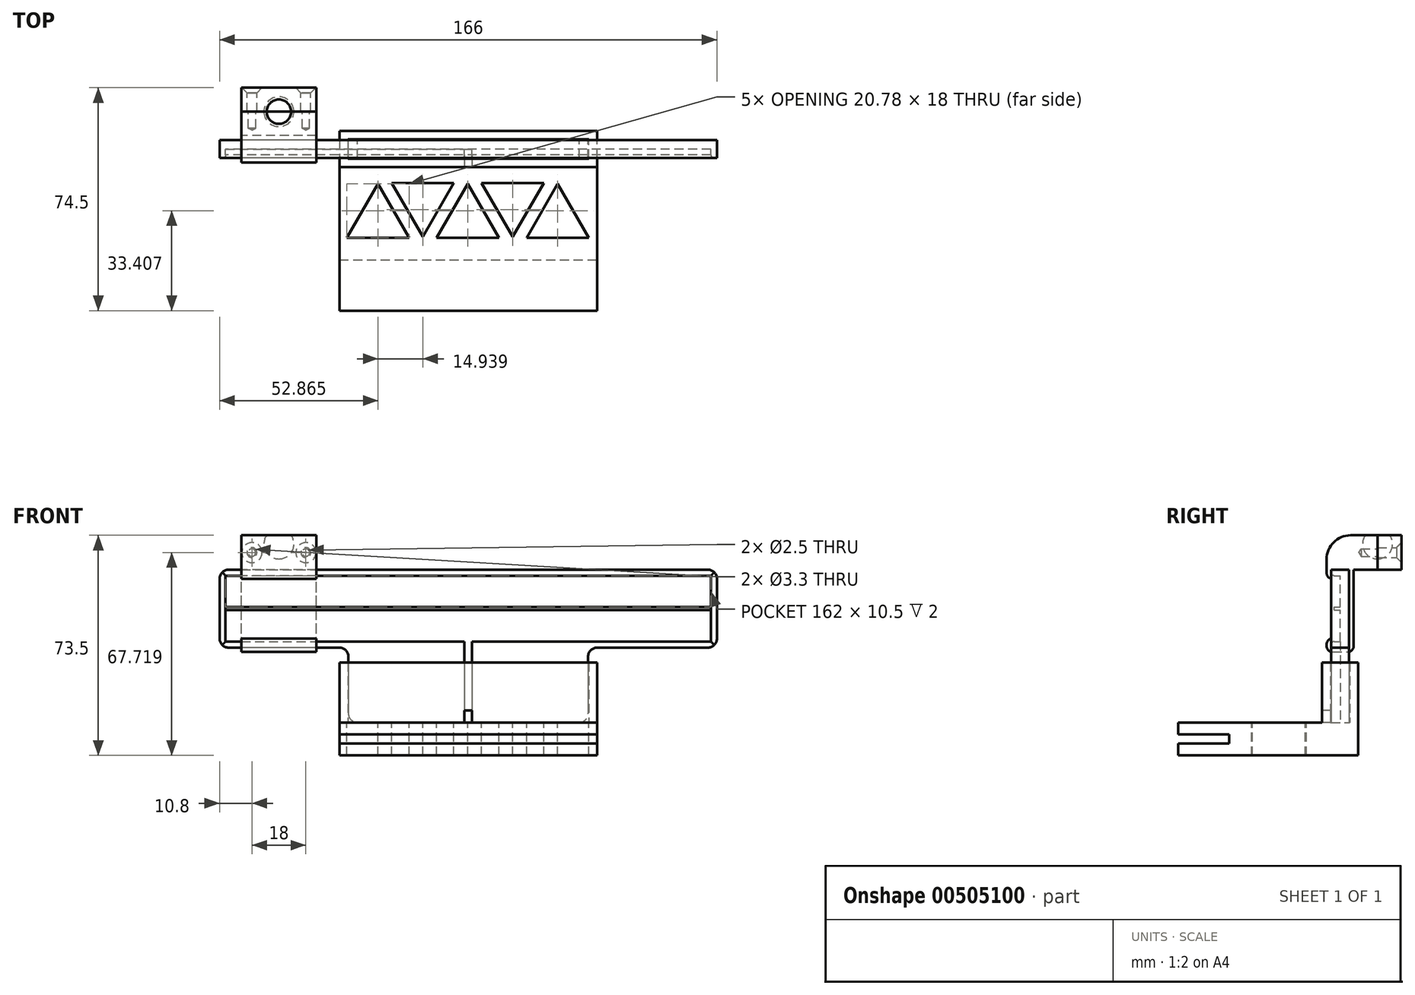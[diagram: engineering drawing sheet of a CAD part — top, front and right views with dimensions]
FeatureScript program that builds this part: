
annotation { "Feature Type Name" : "Feature", "Feature Type Description" : "" }
export const myFeature = defineFeature(function(context is Context, id is Id, definition is map)
    precondition{}
    {
        {
            var Q0;
            Q0=qCreatedBy(makeId("Front.planeOp"),FACE);
            var sketch = newSketch(context, id + "F0", { "sketchPlane" : qUnion([Q0])});
            skLineSegment(sketch, "E0.bottom", {"start": v(83, -13) * mm, "end": v(-83, -13) * mm});
            skLineSegment(sketch, "E0.top", {"start": v(83, 13) * mm, "end": v(-83, 13) * mm});
            skLineSegment(sketch, "E0.left", {"start": v(83, -13) * mm, "end": v(83, 13) * mm});
            skLineSegment(sketch, "E0.right", {"start": v(-83, -13) * mm, "end": v(-83, 13) * mm});
            skPoint(sketch, "E0.middle", {"position": v(0, 0) * mm});
            skLineSegment(sketch, "E1.bottom", {"start": v(-40, -13) * mm, "end": v(40, -13) * mm});
            skLineSegment(sketch, "E1.top", {"start": v(-40, -38) * mm, "end": v(40, -38) * mm});
            skLineSegment(sketch, "E1.left", {"start": v(-40, -13) * mm, "end": v(-40, -38) * mm});
            skLineSegment(sketch, "E1.right", {"start": v(40, -13) * mm, "end": v(40, -38) * mm});
            skSolve(sketch);
        }
        {
            var Q0;
            Q0 = qSketchRegion(id + "F0", true);
            extrude(context, id + "F1", {"entities" : qUnion([Q0]), "depth" : 3 * mm});
        }
        {
            var Q0;
            Q0=makeQuery(id+"F1.opExtrude","CAP_FACE",FACE,{"disambiguationData":[OSD([sQuery(id+"F0.wireOp",EDGE,"E0.bottom"),sQuery(id+"F0.wireOp",EDGE,"E0.top"),sQuery(id+"F0.wireOp",EDGE,"E0.left"),sQuery(id+"F0.wireOp",EDGE,"E0.right"),sQuery(id+"F0.wireOp",EDGE,"ytznH25m-S5ns-YEqi-e5KJ-ufFRk47Cag2v.top"),sQuery(id+"F0.wireOp",EDGE,"ytznH25m-S5ns-YEqi-e5KJ-ufFRk47Cag2v.left"),sQuery(id+"F0.wireOp",EDGE,"ytznH25m-S5ns-YEqi-e5KJ-ufFRk47Cag2v.right"),sQuery(id+"F0.wireOp",EDGE,"df92ae9d-98ef-4524-ba73-5d8abbe1a62c0.MirrorCS"),sQuery(id+"F0.wireOp",EDGE,"cedffd24-c050-4cca-8132-216843a770b10.MirrorCS"),sQuery(id+"F0.wireOp",EDGE,"234c480e-fd0d-4cc7-8f42-385ae9078e1c0.MirrorCS")])],"isStart":false});
            var sketch = newSketch(context, id + "F2", { "sketchPlane" : qUnion([Q0])});
            skLineSegment(sketch, "E2.0", {"start": v(83, 13) * mm, "end": v(-83, 13) * mm});
            skLineSegment(sketch, "E3.0", {"start": v(-83, -13) * mm, "end": v(-83, 13) * mm});
            skLineSegment(sketch, "E4.0", {"start": v(-40, -13) * mm, "end": v(-83, -13) * mm});
            skLineSegment(sketch, "E5.0", {"start": v(83, -13) * mm, "end": v(40, -13) * mm});
            skLineSegment(sketch, "E6.0", {"start": v(83, -13) * mm, "end": v(83, 13) * mm});
            skLineSegment(sketch, "E7.0", {"start": v(40, -13) * mm, "end": v(40, -38) * mm});
            skLineSegment(sketch, "E8.0", {"start": v(-40, -13) * mm, "end": v(-40, -38) * mm});
            skLineSegment(sketch, "E9.0", {"start": v(-40, -11) * mm, "end": v(-81, -11) * mm});
            skLineSegment(sketch, "E9.1", {"start": v(81, -11) * mm, "end": v(40, -11) * mm});
            skLineSegment(sketch, "E9.2", {"start": v(81, -11) * mm, "end": v(81, 11) * mm});
            skLineSegment(sketch, "E9.3", {"start": v(81, 11) * mm, "end": v(-81, 11) * mm});
            skLineSegment(sketch, "E9.4", {"start": v(-81, -11) * mm, "end": v(-81, 11) * mm});
            skLineSegment(sketch, "E10", {"start": v(-40, -11) * mm, "end": v(-1.25, -11) * mm});
            skLineSegment(sketch, "E11", {"start": v(-1.25, -11) * mm, "end": v(-1.25, -38) * mm});
            skLineSegment(sketch, "E12", {"start": v(-1.25, -38) * mm, "end": v(-40, -38) * mm});
            skLineSegment(sketch, "E13", {"start": v(40, -11) * mm, "end": v(1.25, -11) * mm});
            skLineSegment(sketch, "E14", {"start": v(1.25, -11) * mm, "end": v(1.25, -38) * mm});
            skLineSegment(sketch, "E15", {"start": v(1.25, -38) * mm, "end": v(40, -38) * mm});
            skSolve(sketch);
        }
        {
            var Q0;
            Q0 = qSketchRegion(id + "F2", true);
            extrude(context, id + "F3", {"entities" : qUnion([Q0]), "operationType" : NewBodyOperationType.ADD, "depth" : 3 * mm});
        }
        {
            var Q0;
            Q0=makeQuery(id+"F1.opExtrude","CAP_FACE",FACE,{"disambiguationData":[OSD([sQuery(id+"F0.wireOp",EDGE,"E0.bottom"),sQuery(id+"F0.wireOp",EDGE,"E0.top"),sQuery(id+"F0.wireOp",EDGE,"E0.left"),sQuery(id+"F0.wireOp",EDGE,"E0.right"),sQuery(id+"F0.wireOp",EDGE,"E1.top"),sQuery(id+"F0.wireOp",EDGE,"E1.left"),sQuery(id+"F0.wireOp",EDGE,"E1.right")])],"isStart":false});
            var sketch = newSketch(context, id + "F4", { "sketchPlane" : qUnion([Q0])});
            skLineSegment(sketch, "E16.bottom", {"start": v(81, -0.5) * mm, "end": v(-81, -0.5) * mm});
            skLineSegment(sketch, "E16.top", {"start": v(81, 0.5) * mm, "end": v(-81, 0.5) * mm});
            skLineSegment(sketch, "E16.left", {"start": v(81, -0.5) * mm, "end": v(81, 0.5) * mm});
            skLineSegment(sketch, "E16.right", {"start": v(-81, -0.5) * mm, "end": v(-81, 0.5) * mm});
            skPoint(sketch, "E16.middle", {"position": v(0, 0) * mm});
            skSolve(sketch);
        }
        {
            var Q0;
            Q0 = qSketchRegion(id + "F4", true);
            extrude(context, id + "F5", {"entities" : qUnion([Q0]), "operationType" : NewBodyOperationType.ADD, "depth" : 2 * mm});
        }
        {
            var Q0;
            Q0=makeQuery(id+"F3.boolean.opBoolean","MERGE",EDGE,{"derivedFrom":[makeQuery(id+"F1.opExtrude","SWEPT_EDGE",EDGE,{"disambiguationData":[OSD([sQuery(id+"F0.wireOp",EDGE,"E0.top"),sQuery(id+"F0.wireOp",EDGE,"E0.left")])]}),makeQuery(id+"F3.opExtrude","SWEPT_EDGE",EDGE,{"disambiguationData":[OSD([sQuery(id+"F2.wireOp",EDGE,"E2.0"),sQuery(id+"F2.wireOp",EDGE,"E6.0")])]})]});
            var Q1;
            Q1=makeQuery(id+"F3.boolean.opBoolean","MERGE",EDGE,{"derivedFrom":[makeQuery(id+"F1.opExtrude","SWEPT_EDGE",EDGE,{"disambiguationData":[OSD([sQuery(id+"F0.wireOp",EDGE,"E0.bottom"),sQuery(id+"F0.wireOp",EDGE,"E0.left")])]}),makeQuery(id+"F3.opExtrude","SWEPT_EDGE",EDGE,{"disambiguationData":[OSD([sQuery(id+"F2.wireOp",EDGE,"E5.0"),sQuery(id+"F2.wireOp",EDGE,"E6.0")])]})]});
            var Q2;
            Q2=makeQuery(id+"F3.boolean.opBoolean","MERGE",EDGE,{"derivedFrom":[makeQuery(id+"F1.opExtrude","SWEPT_EDGE",EDGE,{"disambiguationData":[OSD([sQuery(id+"F0.wireOp",EDGE,"E0.bottom"),sQuery(id+"F0.wireOp",EDGE,"E1.bottom"),sQuery(id+"F0.wireOp",EDGE,"E1.right")])]}),makeQuery(id+"F3.opExtrude","SWEPT_EDGE",EDGE,{"disambiguationData":[OSD([sQuery(id+"F2.wireOp",EDGE,"E5.0"),sQuery(id+"F2.wireOp",EDGE,"E7.0")])]})]});
            var Q3;
            Q3=makeQuery(id+"F3.boolean.opBoolean","MERGE",EDGE,{"derivedFrom":[makeQuery(id+"F1.opExtrude","SWEPT_EDGE",EDGE,{"disambiguationData":[OSD([sQuery(id+"F0.wireOp",EDGE,"E0.bottom"),sQuery(id+"F0.wireOp",EDGE,"E1.bottom"),sQuery(id+"F0.wireOp",EDGE,"E1.left")])]}),makeQuery(id+"F3.opExtrude","SWEPT_EDGE",EDGE,{"disambiguationData":[OSD([sQuery(id+"F2.wireOp",EDGE,"E4.0"),sQuery(id+"F2.wireOp",EDGE,"E8.0")])]})]});
            var Q4;
            Q4=makeQuery(id+"F3.boolean.opBoolean","MERGE",EDGE,{"derivedFrom":[makeQuery(id+"F1.opExtrude","SWEPT_EDGE",EDGE,{"disambiguationData":[OSD([sQuery(id+"F0.wireOp",EDGE,"E0.bottom"),sQuery(id+"F0.wireOp",EDGE,"E0.right")])]}),makeQuery(id+"F3.opExtrude","SWEPT_EDGE",EDGE,{"disambiguationData":[OSD([sQuery(id+"F2.wireOp",EDGE,"E3.0"),sQuery(id+"F2.wireOp",EDGE,"E4.0")])]})]});
            var Q5;
            Q5=makeQuery(id+"F3.boolean.opBoolean","MERGE",EDGE,{"derivedFrom":[makeQuery(id+"F1.opExtrude","SWEPT_EDGE",EDGE,{"disambiguationData":[OSD([sQuery(id+"F0.wireOp",EDGE,"E0.top"),sQuery(id+"F0.wireOp",EDGE,"E0.right")])]}),makeQuery(id+"F3.opExtrude","SWEPT_EDGE",EDGE,{"disambiguationData":[OSD([sQuery(id+"F2.wireOp",EDGE,"E2.0"),sQuery(id+"F2.wireOp",EDGE,"E3.0")])]})]});
            var Q6;
            Q6=makeQuery(id+"F3.boolean.opBoolean","MERGE",EDGE,{"derivedFrom":[makeQuery(id+"F1.opExtrude","SWEPT_EDGE",EDGE,{"disambiguationData":[OSD([sQuery(id+"F0.wireOp",EDGE,"E1.top"),sQuery(id+"F0.wireOp",EDGE,"E1.right")])]}),makeQuery(id+"F3.opExtrude","SWEPT_EDGE",EDGE,{"disambiguationData":[OSD([sQuery(id+"F2.wireOp",EDGE,"E7.0"),sQuery(id+"F2.wireOp",EDGE,"E15")])]})]});
            var Q7;
            Q7=makeQuery(id+"F3.boolean.opBoolean","MERGE",EDGE,{"derivedFrom":[makeQuery(id+"F1.opExtrude","SWEPT_EDGE",EDGE,{"disambiguationData":[OSD([sQuery(id+"F0.wireOp",EDGE,"E1.top"),sQuery(id+"F0.wireOp",EDGE,"E1.left")])]}),makeQuery(id+"F3.opExtrude","SWEPT_EDGE",EDGE,{"disambiguationData":[OSD([sQuery(id+"F2.wireOp",EDGE,"E8.0"),sQuery(id+"F2.wireOp",EDGE,"E12")])]})]});
            fillet(context, id + "F6", {"entities" : qUnion([Q0, Q1, Q2, Q3, Q4, Q5, Q6, Q7]), "radius" : 3 * mm, "tangentPropagation" : true, "allowEdgeOverflow" : false});
        }
        {
            var Q0;
            Q0=makeQuery(id+"F3.opExtrude","CAP_EDGE",EDGE,{"disambiguationData":[OSD([sQuery(id+"F2.wireOp",EDGE,"E9.3")])],"isStart":false});
            var Q1;
            Q1=makeQuery(id+"F3.opExtrude","CAP_EDGE",EDGE,{"disambiguationData":[OSD([sQuery(id+"F2.wireOp",EDGE,"E9.4")])],"isStart":false});
            var Q2;
            Q2=makeQuery(id+"F3.opExtrude","CAP_EDGE",EDGE,{"disambiguationData":[OSD([sQuery(id+"F2.wireOp",EDGE,"E9.0"),sQuery(id+"F2.wireOp",EDGE,"E10")])],"isStart":false});
            var Q3;
            Q3=makeQuery(id+"F3.opExtrude","CAP_EDGE",EDGE,{"disambiguationData":[OSD([sQuery(id+"F2.wireOp",EDGE,"E9.1"),sQuery(id+"F2.wireOp",EDGE,"E13")])],"isStart":false});
            var Q4;
            Q4=makeQuery(id+"F3.opExtrude","CAP_EDGE",EDGE,{"disambiguationData":[OSD([sQuery(id+"F2.wireOp",EDGE,"E9.2")])],"isStart":false});
            fillet(context, id + "F7", {"entities" : qUnion([Q0, Q1, Q2, Q3, Q4]), "radius" : 1 * mm, "tangentPropagation" : true, "allowEdgeOverflow" : false});
        }
        {
            var Q0;
            Q0=makeQuery(id+"F3.boolean.opBoolean","MERGE",FACE,{"derivedFrom":[makeQuery(id+"F1.opExtrude","SWEPT_FACE",FACE,{"disambiguationData":[OSD([sQuery(id+"F0.wireOp",EDGE,"E1.top")])]}),makeQuery(id+"F3.opExtrude","SWEPT_FACE",FACE,{"disambiguationData":[OSD([sQuery(id+"F2.wireOp",EDGE,"E12")])]}),makeQuery(id+"F3.opExtrude","SWEPT_FACE",FACE,{"disambiguationData":[OSD([sQuery(id+"F2.wireOp",EDGE,"E15")])]})]});
            var sketch = newSketch(context, id + "F8", { "sketchPlane" : qUnion([Q0])});
            skLineSegment(sketch, "E17.0", {"start": v(1.25, 9) * mm, "end": v(37, 9) * mm});
            skLineSegment(sketch, "E17.1", {"start": v(1.25, 9) * mm, "end": v(-1.25, 9) * mm});
            skLineSegment(sketch, "E17.2", {"start": v(37, 9) * mm, "end": v(43, 9) * mm});
            skLineSegment(sketch, "E17.3", {"start": v(-37, 9) * mm, "end": v(-1.25, 9) * mm});
            skLineSegment(sketch, "E17.4", {"start": v(-43, 9) * mm, "end": v(-37, 9) * mm});
            skLineSegment(sketch, "E17.5", {"start": v(-43, -3) * mm, "end": v(-43, 9) * mm});
            skLineSegment(sketch, "E17.6", {"start": v(43, 9) * mm, "end": v(43, -3) * mm});
            skLineSegment(sketch, "E17.7", {"start": v(43, -3) * mm, "end": v(37, -3) * mm});
            skLineSegment(sketch, "E17.8", {"start": v(-37, -3) * mm, "end": v(37, -3) * mm});
            skLineSegment(sketch, "E17.9", {"start": v(-37, -3) * mm, "end": v(-43, -3) * mm});
            skLineSegment(sketch, "E18.0", {"start": v(-37, 6.2) * mm, "end": v(-1.25, 6.2) * mm});
            skLineSegment(sketch, "E18.1", {"start": v(-40.2, 6.2) * mm, "end": v(-37, 6.2) * mm});
            skLineSegment(sketch, "E18.2", {"start": v(-40.2, -0.2) * mm, "end": v(-40.2, 6.2) * mm});
            skLineSegment(sketch, "E18.3", {"start": v(-37, -0.2) * mm, "end": v(-40.2, -0.2) * mm});
            skLineSegment(sketch, "E18.4", {"start": v(-37, -0.2) * mm, "end": v(37, -0.2) * mm});
            skLineSegment(sketch, "E18.5", {"start": v(1.25, 6.2) * mm, "end": v(37, 6.2) * mm});
            skLineSegment(sketch, "E18.6", {"start": v(37, 6.2) * mm, "end": v(40.2, 6.2) * mm});
            skLineSegment(sketch, "E18.7", {"start": v(40.2, 6.2) * mm, "end": v(40.2, -0.2) * mm});
            skLineSegment(sketch, "E18.8", {"start": v(40.2, -0.2) * mm, "end": v(37, -0.2) * mm});
            skLineSegment(sketch, "E19", {"start": v(1.25, 6.2) * mm, "end": v(-1.25, 6.2) * mm});
            skSolve(sketch);
        }
        {
            var Q0;
            Q0 = qSketchRegion(id + "F8", true);
            extrude(context, id + "F9", {"entities" : qUnion([Q0]), "oppositeDirection" : true, "depth" : 20 * mm});
        }
        {
            var Q0;
            Q0=makeQuery(id+"F9.opExtrude","CAP_FACE",FACE,{"disambiguationData":[OSD([sQuery(id+"F8.wireOp",EDGE,"8f80f519-4c1a-4023-b6a8-295c1c52ba16.0"),sQuery(id+"F8.wireOp",EDGE,"08e55738-1a8b-462c-8b5f-6e2352a6861a.0"),sQuery(id+"F8.wireOp",EDGE,"df1ae1b3-9407-48c6-8a92-31e4def18985.0"),sQuery(id+"F8.wireOp",EDGE,"7d09f095-180c-42f7-a629-e3ec4bffc7fb.0"),sQuery(id+"F8.wireOp",EDGE,"688b7f32-6940-423c-993a-f274958fdb2f.0"),sQuery(id+"F8.wireOp",EDGE,"d8653beb-2f90-41c1-82e6-8edcaac2620c.0"),sQuery(id+"F8.wireOp",EDGE,"a51acf63-bb40-4388-a766-018fd9339a70.0"),sQuery(id+"F8.wireOp",EDGE,"03a022a2-261d-486d-8482-124d5ba834bb.0"),sQuery(id+"F8.wireOp",EDGE,"Rfw31xpp-0EbB-aFLx-32cb-AFAiJERe9Qdi"),sQuery(id+"F8.wireOp",EDGE,"87e0dc2d-6d3b-407e-9d83-58cfb59100ee.0"),sQuery(id+"F8.wireOp",EDGE,"E17.0"),sQuery(id+"F8.wireOp",EDGE,"E17.1"),sQuery(id+"F8.wireOp",EDGE,"E17.2"),sQuery(id+"F8.wireOp",EDGE,"E17.3"),sQuery(id+"F8.wireOp",EDGE,"E17.4"),sQuery(id+"F8.wireOp",EDGE,"E17.5"),sQuery(id+"F8.wireOp",EDGE,"E17.6"),sQuery(id+"F8.wireOp",EDGE,"E17.7"),sQuery(id+"F8.wireOp",EDGE,"E17.8"),sQuery(id+"F8.wireOp",EDGE,"E17.9")])],"isStart":true});
            var sketch = newSketch(context, id + "F10", { "sketchPlane" : qUnion([Q0])});
            skLineSegment(sketch, "E20.0.0", {"start": v(-43, -3) * mm, "end": v(43, -3) * mm});
            skLineSegment(sketch, "E20.0.1", {"start": v(43, -3) * mm, "end": v(43, 9) * mm});
            skLineSegment(sketch, "E20.0.2", {"start": v(43, 9) * mm, "end": v(-43, 9) * mm});
            skLineSegment(sketch, "E20.0.3", {"start": v(-43, 9) * mm, "end": v(-43, -3) * mm});
            skSolve(sketch);
        }
        {
            var Q0;
            Q0 = qSketchRegion(id + "F10", true);
            extrude(context, id + "F11", {"entities" : qUnion([Q0]), "operationType" : NewBodyOperationType.ADD, "depth" : 2 * mm});
        }
        {
            var Q0;
            Q0=makeQuery(id+"F9.opExtrude","SWEPT_FACE",FACE,{"disambiguationData":[OSD([sQuery(id+"F8.wireOp",EDGE,"E17.0"),sQuery(id+"F8.wireOp",EDGE,"E17.1"),sQuery(id+"F8.wireOp",EDGE,"E17.2"),sQuery(id+"F8.wireOp",EDGE,"E17.3"),sQuery(id+"F8.wireOp",EDGE,"E17.4")])]});
            var sketch = newSketch(context, id + "F12", { "sketchPlane" : qUnion([Q0])});
            skPoint(sketch, "E21.0", {"position": v(1.25, -38) * mm});
            skPoint(sketch, "E22.0", {"position": v(-1.25, -38) * mm});
            skLineSegment(sketch, "E23.bottom", {"start": v(1.25, -38) * mm, "end": v(-1.25, -38) * mm});
            skLineSegment(sketch, "E23.top", {"start": v(1.25, -34) * mm, "end": v(-1.25, -34) * mm});
            skLineSegment(sketch, "E23.left", {"start": v(1.25, -38) * mm, "end": v(1.25, -34) * mm});
            skLineSegment(sketch, "E23.right", {"start": v(-1.25, -38) * mm, "end": v(-1.25, -34) * mm});
            skSolve(sketch);
        }
        {
            var Q0;
            Q0 = qSketchRegion(id + "F12", true);
            extrude(context, id + "F13", {"entities" : qUnion([Q0]), "operationType" : NewBodyOperationType.REMOVE, "oppositeDirection" : true, "depth" : 4 * mm});
        }
        {
            var Q0;
            Q0=makeQuery(id+"F11.opExtrude","CAP_FACE",FACE,{"disambiguationData":[OSD([sQuery(id+"F10.wireOp",EDGE,"E20.0.0"),sQuery(id+"F10.wireOp",EDGE,"E20.0.1"),sQuery(id+"F10.wireOp",EDGE,"E20.0.2"),sQuery(id+"F10.wireOp",EDGE,"E20.0.3")])],"isStart":false});
            var sketch = newSketch(context, id + "F14", { "sketchPlane" : qUnion([Q0])});
            skPoint(sketch, "E24.0", {"position": v(43, -3) * mm});
            skPoint(sketch, "E25.0", {"position": v(-43, -3) * mm});
            skLineSegment(sketch, "E26.bottom", {"start": v(43, -3) * mm, "end": v(-43, -3) * mm});
            skLineSegment(sketch, "E26.top", {"start": v(43, 57) * mm, "end": v(-43, 57) * mm});
            skLineSegment(sketch, "E26.left", {"start": v(43, -3) * mm, "end": v(43, 57) * mm});
            skLineSegment(sketch, "E26.right", {"start": v(-43, -3) * mm, "end": v(-43, 57) * mm});
            skSolve(sketch);
        }
        {
            var Q0;
            Q0 = qSketchRegion(id + "F14", true);
            extrude(context, id + "F15", {"entities" : qUnion([Q0]), "operationType" : NewBodyOperationType.ADD, "endBound" : BoundingType.SYMMETRIC, "depth" : 4 * mm});
        }
        {
            var Q0;
            Q0=makeQuery(id+"F15.opExtrude","CAP_FACE",FACE,{"disambiguationData":[OSD([sQuery(id+"F14.wireOp",EDGE,"E26.bottom"),sQuery(id+"F14.wireOp",EDGE,"E26.top"),sQuery(id+"F14.wireOp",EDGE,"E26.left"),sQuery(id+"F14.wireOp",EDGE,"E26.right")])],"isStart":false});
            var sketch = newSketch(context, id + "F16", { "sketchPlane" : qUnion([Q0])});
            skLineSegment(sketch, "E27", {"start": v(-43, 0) * mm, "end": v(-43, 40) * mm});
            skLineSegment(sketch, "E28", {"start": v(-43, 40) * mm, "end": v(43, 40) * mm});
            skLineSegment(sketch, "E29", {"start": v(43, 40) * mm, "end": v(43, 0) * mm});
            skLineSegment(sketch, "E30.0", {"start": v(43, -3) * mm, "end": v(-43, -3) * mm});
            skLineSegment(sketch, "E31", {"start": v(-43, 0) * mm, "end": v(-43, -3) * mm});
            skLineSegment(sketch, "E32", {"start": v(43, -3) * mm, "end": v(43, 0) * mm});
            skSolve(sketch);
        }
        {
            var Q0;
            Q0 = qSketchRegion(id + "F16", true);
            extrude(context, id + "F17", {"entities" : qUnion([Q0]), "operationType" : NewBodyOperationType.ADD, "depth" : 3 * mm});
        }
        {
            var Q0;
            Q0=makeQuery(id+"F17.opExtrude","CAP_FACE",FACE,{"disambiguationData":[OSD([sQuery(id+"F16.wireOp",EDGE,"f466e9dd-5a19-49e1-9c5d-092f5ca6e284.0"),sQuery(id+"F16.wireOp",EDGE,"26d59c0c-0793-47e5-85c4-0c295c787126.0"),sQuery(id+"F16.wireOp",EDGE,"70284398-0f37-47e1-91d1-e00cf8cfd432.0"),sQuery(id+"F16.wireOp",EDGE,"E27"),sQuery(id+"F16.wireOp",EDGE,"E28"),sQuery(id+"F16.wireOp",EDGE,"E29")])],"isStart":false});
            var sketch = newSketch(context, id + "F18", { "sketchPlane" : qUnion([Q0])});
            skLineSegment(sketch, "E33.0.0", {"start": v(43, 40) * mm, "end": v(-43, 40) * mm});
            skLineSegment(sketch, "E33.0.1", {"start": v(-43, 40) * mm, "end": v(-43, -3) * mm});
            skLineSegment(sketch, "E33.0.2", {"start": v(-43, -3) * mm, "end": v(43, -3) * mm});
            skLineSegment(sketch, "E33.0.3", {"start": v(43, -3) * mm, "end": v(43, 40) * mm});
            skLineSegment(sketch, "E34.0.0", {"start": v(-43, 57) * mm, "end": v(-43, 40) * mm});
            skLineSegment(sketch, "E34.0.1", {"start": v(-43, 40) * mm, "end": v(43, 40) * mm});
            skLineSegment(sketch, "E34.0.2", {"start": v(43, 40) * mm, "end": v(43, 57) * mm});
            skLineSegment(sketch, "E34.0.3", {"start": v(43, 57) * mm, "end": v(-43, 57) * mm});
            skSolve(sketch);
        }
        {
            var Q0;
            Q0 = qSketchRegion(id + "F18", true);
            extrude(context, id + "F19", {"entities" : qUnion([Q0]), "operationType" : NewBodyOperationType.ADD, "depth" : 4 * mm});
        }
        {
            var Q0;
            Q0=makeQuery(id+"F15.boolean.opBoolean","MERGE",FACE,{"derivedFrom":[makeQuery(id+"F13.boolean.opBoolean","MERGE",FACE,{"derivedFrom":[makeQuery(id+"F11.opExtrude","CAP_FACE",FACE,{"disambiguationData":[OSD([sQuery(id+"F10.wireOp",EDGE,"E20.0.0"),sQuery(id+"F10.wireOp",EDGE,"E20.0.1"),sQuery(id+"F10.wireOp",EDGE,"E20.0.2"),sQuery(id+"F10.wireOp",EDGE,"E20.0.3")])],"isStart":true}),makeQuery(id+"F13.opExtrude","SWEPT_FACE",FACE,{"disambiguationData":[OSD([sQuery(id+"F12.wireOp",EDGE,"E23.bottom")])]})]}),makeQuery(id+"F15.opExtrude","CAP_FACE",FACE,{"disambiguationData":[OSD([sQuery(id+"F14.wireOp",EDGE,"E26.bottom"),sQuery(id+"F14.wireOp",EDGE,"E26.top"),sQuery(id+"F14.wireOp",EDGE,"E26.left"),sQuery(id+"F14.wireOp",EDGE,"E26.right")])],"isStart":true})]});
            var sketch = newSketch(context, id + "F20", { "sketchPlane" : qUnion([Q0])});
            skCircle(sketch, "E35.cCircle", {"center": v(-30.13, -26.6) * mm, "radius": 6 * mm, "construction": true});
            skLineSegment(sketch, "E35.0", {"start": v(-19.74, -32.6) * mm, "end": v(-40.53, -32.6) * mm});
            skLineSegment(sketch, "E35.1", {"start": v(-40.53, -32.6) * mm, "end": v(-30.13, -14.6) * mm});
            skLineSegment(sketch, "E35.2", {"start": v(-30.13, -14.6) * mm, "end": v(-19.74, -32.6) * mm});
            skPoint(sketch, "E35.0.midPoint", {"position": v(-30.13, -32.6) * mm});
            skLineSegment(sketch, "E36", {"start": v(-30.13, -14.6) * mm, "end": v(-30.13, -32.6) * mm, "construction": true});
            skCircle(sketch, "E37.1.0.0", {"center": v(-0.13, -26.6) * mm, "radius": 6 * mm, "construction": true});
            skLineSegment(sketch, "E37.1.0.1", {"start": v(10.26, -32.6) * mm, "end": v(-10.53, -32.6) * mm});
            skLineSegment(sketch, "E37.1.0.2", {"start": v(-10.53, -32.6) * mm, "end": v(-0.13, -14.6) * mm});
            skLineSegment(sketch, "E37.1.0.3", {"start": v(-0.13, -14.6) * mm, "end": v(-0.13, -32.6) * mm, "construction": true});
            skLineSegment(sketch, "E37.1.0.4", {"start": v(-0.13, -14.6) * mm, "end": v(10.26, -32.6) * mm});
            skPoint(sketch, "E37.1.0.5", {"position": v(-0.13, -32.6) * mm});
            skCircle(sketch, "E37.2.0.0", {"center": v(29.87, -26.6) * mm, "radius": 6 * mm, "construction": true});
            skLineSegment(sketch, "E37.2.0.1", {"start": v(40.26, -32.6) * mm, "end": v(19.47, -32.6) * mm});
            skLineSegment(sketch, "E37.2.0.2", {"start": v(19.47, -32.6) * mm, "end": v(29.87, -14.6) * mm});
            skLineSegment(sketch, "E37.2.0.3", {"start": v(29.87, -14.6) * mm, "end": v(29.87, -32.6) * mm, "construction": true});
            skLineSegment(sketch, "E37.2.0.4", {"start": v(29.87, -14.6) * mm, "end": v(40.26, -32.6) * mm});
            skPoint(sketch, "E37.2.0.5", {"position": v(29.87, -32.6) * mm});
            skLineSegment(sketch, "E37.direction1", {"start": v(-40.53, -32.6) * mm, "end": v(-10.53, -32.6) * mm, "construction": true});
            skCircle(sketch, "E38.cCircle", {"center": v(-15.2, -20.28) * mm, "radius": 6 * mm, "construction": true});
            skLineSegment(sketch, "E38.0", {"start": v(-25.59, -14.28) * mm, "end": v(-4.8, -14.28) * mm});
            skLineSegment(sketch, "E38.1", {"start": v(-4.8, -14.28) * mm, "end": v(-15.2, -32.28) * mm});
            skLineSegment(sketch, "E38.2", {"start": v(-15.2, -32.28) * mm, "end": v(-25.59, -14.28) * mm});
            skPoint(sketch, "E38.0.midPoint", {"position": v(-15.2, -14.28) * mm});
            skLineSegment(sketch, "E39", {"start": v(-15.2, -32.28) * mm, "end": v(-15.2, -14.28) * mm, "construction": true});
            skLineSegment(sketch, "E40.1.0.0", {"start": v(4.41, -14.28) * mm, "end": v(25.2, -14.28) * mm});
            skLineSegment(sketch, "E40.1.0.1", {"start": v(14.8, -32.28) * mm, "end": v(4.41, -14.28) * mm});
            skLineSegment(sketch, "E40.1.0.2", {"start": v(25.2, -14.28) * mm, "end": v(14.8, -32.28) * mm});
            skLineSegment(sketch, "E40.direction1", {"start": v(-25.59, -14.28) * mm, "end": v(4.41, -14.28) * mm, "construction": true});
            skSolve(sketch);
        }
        {
            var Q0;
            Q0 = qSketchRegion(id + "F20", true);
            extrude(context, id + "F21", {"entities" : qUnion([Q0]), "operationType" : NewBodyOperationType.REMOVE, "oppositeDirection" : true, "depth" : 50 * mm});
        }
        {
            var Q0;
            Q0=qCreatedBy(makeId("Right.planeOp"),FACE);
            var sketch = newSketch(context, id + "F22", { "sketchPlane" : qUnion([Q0])});
            skLineSegment(sketch, "E41.0", {"start": v(0, 13) * mm, "end": v(-6, 13) * mm});
            skLineSegment(sketch, "E42.0", {"start": v(-6, 13) * mm, "end": v(-6, 10) * mm});
            skLineSegment(sketch, "E43.0", {"start": v(0, -10) * mm, "end": v(0, 10) * mm});
            skLineSegment(sketch, "E44.0", {"start": v(0, 10) * mm, "end": v(0, 13) * mm});
            skLineSegment(sketch, "E45.0", {"start": v(0, -13) * mm, "end": v(0, -10) * mm});
            skLineSegment(sketch, "E46.0", {"start": v(-6, -13) * mm, "end": v(0, -13) * mm});
            skLineSegment(sketch, "E47.0", {"start": v(-6, -10) * mm, "end": v(-6, -13) * mm});
            skLineSegment(sketch, "E48.0", {"start": v(-7.5, 14.5) * mm, "end": v(-7.5, 10) * mm});
            skLineSegment(sketch, "E48.1", {"start": v(1.5, 14.5) * mm, "end": v(-7.5, 14.5) * mm});
            skLineSegment(sketch, "E48.2", {"start": v(1.5, 10) * mm, "end": v(1.5, 14.5) * mm});
            skLineSegment(sketch, "E48.3", {"start": v(-7.5, -10) * mm, "end": v(-7.5, -14.5) * mm});
            skLineSegment(sketch, "E48.4", {"start": v(-7.5, -14.5) * mm, "end": v(1.5, -14.5) * mm});
            skLineSegment(sketch, "E48.5", {"start": v(1.5, -14.5) * mm, "end": v(1.5, -10) * mm});
            skLineSegment(sketch, "E48.6", {"start": v(1.5, -10) * mm, "end": v(1.5, 10) * mm});
            skLineSegment(sketch, "E49", {"start": v(-7.5, 10) * mm, "end": v(-6, 10) * mm});
            skLineSegment(sketch, "E50", {"start": v(-7.5, -10) * mm, "end": v(-6, -10) * mm});
            skSolve(sketch);
        }
        {
            var Q0;
            Q0 = qSketchRegion(id + "F22", true);
            extrude(context, id + "F23", {"entities" : qUnion([Q0]), "depth" : 25 * mm});
        }
        {
            var Q0;
            Q0=makeQuery(id+"F23.opExtrude","SWEPT_BODY",BODY,{"disambiguationData":[OSD([sQuery(id+"F22.wireOp",EDGE,"E41.0"),sQuery(id+"F22.wireOp",EDGE,"E42.0"),sQuery(id+"F22.wireOp",EDGE,"E43.0"),sQuery(id+"F22.wireOp",EDGE,"E44.0"),sQuery(id+"F22.wireOp",EDGE,"E45.0"),sQuery(id+"F22.wireOp",EDGE,"E46.0"),sQuery(id+"F22.wireOp",EDGE,"E47.0"),sQuery(id+"F22.wireOp",EDGE,"E48.0"),sQuery(id+"F22.wireOp",EDGE,"E48.1"),sQuery(id+"F22.wireOp",EDGE,"E48.2"),sQuery(id+"F22.wireOp",EDGE,"E48.3"),sQuery(id+"F22.wireOp",EDGE,"E48.4"),sQuery(id+"F22.wireOp",EDGE,"E48.5"),sQuery(id+"F22.wireOp",EDGE,"E48.6"),sQuery(id+"F22.wireOp",EDGE,"E49"),sQuery(id+"F22.wireOp",EDGE,"E50")])]});
            transform(context, id + "F24", {"entities" : qUnion([Q0]), "transformType" : TransformType.TRANSLATION_3D, "dx" : -75.7 * mm, "dy" : 0 * mm, "dz" : 0 * mm, "makeCopy" : false});
        }
        {
            var Q0;
            Q0=makeQuery(id+"F23.opExtrude","SWEPT_FACE",FACE,{"disambiguationData":[OSD([sQuery(id+"F22.wireOp",EDGE,"E48.1")])]});
            var sketch = newSketch(context, id + "F25", { "sketchPlane" : qUnion([Q0])});
            skLineSegment(sketch, "E51.0.0", {"start": v(-75.7, 1.5) * mm, "end": v(-75.7, -7.5) * mm});
            skLineSegment(sketch, "E51.0.1", {"start": v(-75.7, -7.5) * mm, "end": v(-50.7, -7.5) * mm});
            skLineSegment(sketch, "E51.0.2", {"start": v(-50.7, -7.5) * mm, "end": v(-50.7, 1.5) * mm});
            skLineSegment(sketch, "E51.0.3", {"start": v(-50.7, 1.5) * mm, "end": v(-75.7, 1.5) * mm});
            skSolve(sketch);
        }
        {
            var Q0;
            Q0 = qSketchRegion(id + "F25", true);
            extrude(context, id + "F26", {"entities" : qUnion([Q0]), "operationType" : NewBodyOperationType.ADD, "depth" : 10 * mm});
        }
        {
            var Q0;
            Q0=makeQuery(id+"F26.boolean.opBoolean","MERGE",FACE,{"derivedFrom":[makeQuery(id+"F23.opExtrude","SWEPT_FACE",FACE,{"disambiguationData":[OSD([sQuery(id+"F22.wireOp",EDGE,"E48.2"),sQuery(id+"F22.wireOp",EDGE,"E48.5"),sQuery(id+"F22.wireOp",EDGE,"E48.6")])]}),makeQuery(id+"F26.opExtrude","SWEPT_FACE",FACE,{"disambiguationData":[OSD([sQuery(id+"F25.wireOp",EDGE,"E51.0.3")])]})]});
            var sketch = newSketch(context, id + "F27", { "sketchPlane" : qUnion([Q0])});
            skLineSegment(sketch, "E52.bottom", {"start": v(75.7, 24.5) * mm, "end": v(50.7, 24.5) * mm});
            skLineSegment(sketch, "E52.top", {"start": v(75.7, 12.94) * mm, "end": v(50.7, 12.94) * mm});
            skLineSegment(sketch, "E52.left", {"start": v(75.7, 24.5) * mm, "end": v(75.7, 12.94) * mm});
            skLineSegment(sketch, "E52.right", {"start": v(50.7, 24.5) * mm, "end": v(50.7, 12.94) * mm});
            skSolve(sketch);
        }
        {
            var Q0;
            Q0 = qSketchRegion(id + "F27", true);
            extrude(context, id + "F28", {"entities" : qUnion([Q0]), "operationType" : NewBodyOperationType.ADD, "depth" : 8 * mm});
        }
        {
            var Q0;
            Q0=makeQuery(id+"F28.opExtrude","CAP_FACE",FACE,{"disambiguationData":[OSD([sQuery(id+"F27.wireOp",EDGE,"E52.bottom"),sQuery(id+"F27.wireOp",EDGE,"E52.top"),sQuery(id+"F27.wireOp",EDGE,"E52.left"),sQuery(id+"F27.wireOp",EDGE,"E52.right")])],"isStart":false});
            var sketch = newSketch(context, id + "F29", { "sketchPlane" : qUnion([Q0])});
            skLineSegment(sketch, "E53", {"start": v(63.2, 24.5) * mm, "end": v(63.2, -14.5) * mm, "construction": true});
            skArc(sketch, "E54", {"start": v(63.2, 16.6) * mm, "mid": v(68.2, 21.6) * mm, "end": v(63.2, 26.6) * mm});
            skLineSegment(sketch, "E55", {"start": v(63.2, 16.6) * mm, "end": v(63.2, 26.6) * mm});
            skSolve(sketch);
        }
        {
            var Q0;
            {var subQ0=sQuery(id+"F29.wireOp",EDGE,"E55");var subQ1=sQuery(id+"F29.wireOp",EDGE,"E54");var subQ2=makeQuery(id+"F29.imprint","INTERSECT",VERTEX,{"disambiguationData":[OD(0.0)],"derivedFrom":[subQ1,subQ0]});Q0=makeQuery(id+"F29.imprint","IMPRINT",FACE,{"disambiguationData":[TD([[makeQuery(id+"F29.imprint","IMPRINT",EDGE,{"disambiguationData":[TD([[subQ2,-1.0]])],"derivedFrom":subQ1}),1.0]])]});}
            var Q1;
            Q1=sQuery(id+"F29.wireOp",EDGE,"E55");
            revolve(context, id + "F30", {"entities" : qUnion([Q0]), "axis" : qUnion([Q1]), "revolveType" : RevolveType.FULL});
        }
        {
            var Q0;
            Q0=makeQuery(id+"F28.opExtrude","CAP_FACE",FACE,{"disambiguationData":[OSD([sQuery(id+"F27.wireOp",EDGE,"E52.bottom"),sQuery(id+"F27.wireOp",EDGE,"E52.top"),sQuery(id+"F27.wireOp",EDGE,"E52.left"),sQuery(id+"F27.wireOp",EDGE,"E52.right")])],"isStart":false});
            var sketch = newSketch(context, id + "F31", { "sketchPlane" : qUnion([Q0])});
            skLineSegment(sketch, "E56.0.0", {"start": v(50.7, 12.94) * mm, "end": v(75.7, 12.94) * mm});
            skLineSegment(sketch, "E56.0.1", {"start": v(75.7, 12.94) * mm, "end": v(75.7, 24.5) * mm});
            skLineSegment(sketch, "E56.0.2", {"start": v(75.7, 24.5) * mm, "end": v(50.7, 24.5) * mm});
            skLineSegment(sketch, "E56.0.3", {"start": v(50.7, 24.5) * mm, "end": v(50.7, 12.94) * mm});
            skSolve(sketch);
        }
        {
            var Q0;
            Q0 = qSketchRegion(id + "F31", true);
            extrude(context, id + "F32", {"entities" : qUnion([Q0]), "depth" : 8 * mm});
        }
        {
            var Q0;
            Q0=makeQuery(id+"F30.opRevolve","SWEPT_BODY",BODY,{"disambiguationData":[OSD([sQuery(id+"F27.wireOp",EDGE,"E52.bottom"),sQuery(id+"F29.wireOp",EDGE,"E54"),sQuery(id+"F29.wireOp",EDGE,"E55")])]});
            var Q1;
            Q1=makeQuery(id+"F32.opExtrude","SWEPT_BODY",BODY,{"disambiguationData":[OSD([sQuery(id+"F31.wireOp",EDGE,"E56.0.0"),sQuery(id+"F31.wireOp",EDGE,"E56.0.1"),sQuery(id+"F31.wireOp",EDGE,"E56.0.2"),sQuery(id+"F31.wireOp",EDGE,"E56.0.3")])]});
            var Q2;
            Q2=makeQuery(id+"F23.opExtrude","SWEPT_BODY",BODY,{"disambiguationData":[OSD([sQuery(id+"F22.wireOp",EDGE,"E41.0"),sQuery(id+"F22.wireOp",EDGE,"E42.0"),sQuery(id+"F22.wireOp",EDGE,"E43.0"),sQuery(id+"F22.wireOp",EDGE,"E44.0"),sQuery(id+"F22.wireOp",EDGE,"E45.0"),sQuery(id+"F22.wireOp",EDGE,"E46.0"),sQuery(id+"F22.wireOp",EDGE,"E47.0"),sQuery(id+"F22.wireOp",EDGE,"E48.0"),sQuery(id+"F22.wireOp",EDGE,"E48.1"),sQuery(id+"F22.wireOp",EDGE,"E48.2"),sQuery(id+"F22.wireOp",EDGE,"E48.3"),sQuery(id+"F22.wireOp",EDGE,"E48.4"),sQuery(id+"F22.wireOp",EDGE,"E48.5"),sQuery(id+"F22.wireOp",EDGE,"E48.6"),sQuery(id+"F22.wireOp",EDGE,"E49"),sQuery(id+"F22.wireOp",EDGE,"E50")])]});
            booleanBodies(context, id + "F33", {"operationType" : BooleanOperationType.SUBTRACTION, "tools" : qUnion([Q0]), "targets" : qUnion([Q1, Q2])});
        }
        {
            var Q0;
            Q0=makeQuery(id+"F26.opExtrude","CAP_EDGE",EDGE,{"disambiguationData":[OSD([sQuery(id+"F25.wireOp",EDGE,"E51.0.1")])],"isStart":false});
            fillet(context, id + "F34", {"entities" : qUnion([Q0]), "radius" : 8 * mm, "tangentPropagation" : true, "allowEdgeOverflow" : false});
        }
        {
            var Q0;
            Q0=makeQuery(id+"F28.opExtrude","CAP_EDGE",EDGE,{"disambiguationData":[OSD([sQuery(id+"F27.wireOp",EDGE,"E52.top")])],"isStart":true});
            var Q1;
            Q1=makeQuery(id+"F23.opExtrude","SWEPT_EDGE",EDGE,{"disambiguationData":[OSD([sQuery(id+"F22.wireOp",EDGE,"E48.4"),sQuery(id+"F22.wireOp",EDGE,"E48.5")])]});
            var Q2;
            Q2=makeQuery(id+"F23.opExtrude","SWEPT_EDGE",EDGE,{"disambiguationData":[OSD([sQuery(id+"F22.wireOp",EDGE,"E48.3"),sQuery(id+"F22.wireOp",EDGE,"E48.4")])]});
            var Q3;
            Q3=makeQuery(id+"F23.opExtrude","SWEPT_EDGE",EDGE,{"disambiguationData":[OSD([sQuery(id+"F22.wireOp",EDGE,"E48.0"),sQuery(id+"F22.wireOp",EDGE,"E49")])]});
            var Q4;
            Q4=makeQuery(id+"F23.opExtrude","SWEPT_EDGE",EDGE,{"disambiguationData":[OSD([sQuery(id+"F22.wireOp",EDGE,"E48.3"),sQuery(id+"F22.wireOp",EDGE,"E50")])]});
            fillet(context, id + "F35", {"entities" : qUnion([Q0, Q1, Q2, Q3, Q4]), "radius" : 2 * mm, "tangentPropagation" : true, "allowEdgeOverflow" : false});
        }
        {
            var Q0;
            Q0=makeQuery(id+"F32.opExtrude","CAP_FACE",FACE,{"disambiguationData":[OSD([sQuery(id+"F31.wireOp",EDGE,"E56.0.0"),sQuery(id+"F31.wireOp",EDGE,"E56.0.1"),sQuery(id+"F31.wireOp",EDGE,"E56.0.2"),sQuery(id+"F31.wireOp",EDGE,"E56.0.3")])],"isStart":false});
            var sketch = newSketch(context, id + "F36", { "sketchPlane" : qUnion([Q0])});
            skLineSegment(sketch, "E57", {"start": v(75.7, 18.72) * mm, "end": v(50.7, 18.72) * mm, "construction": true});
            skPoint(sketch, "E58", {"position": v(54.2, 18.72) * mm});
            skPoint(sketch, "E59", {"position": v(72.2, 18.72) * mm});
            skLineSegment(sketch, "E60", {"start": v(63.2, 24.5) * mm, "end": v(63.2, 12.94) * mm, "construction": true});
            skSolve(sketch);
        }
        {
            var Q0;
            Q0=sQuery(id+"F36.wireOp",VERTEX,"E58");
            var Q1;
            Q1=sQuery(id+"F36.wireOp",VERTEX,"E59");
            var Q2;
            Q2=makeQuery(id+"F23.opExtrude","SWEPT_BODY",BODY,{"disambiguationData":[OSD([sQuery(id+"F22.wireOp",EDGE,"E41.0"),sQuery(id+"F22.wireOp",EDGE,"E42.0"),sQuery(id+"F22.wireOp",EDGE,"E43.0"),sQuery(id+"F22.wireOp",EDGE,"E44.0"),sQuery(id+"F22.wireOp",EDGE,"E45.0"),sQuery(id+"F22.wireOp",EDGE,"E46.0"),sQuery(id+"F22.wireOp",EDGE,"E47.0"),sQuery(id+"F22.wireOp",EDGE,"E48.0"),sQuery(id+"F22.wireOp",EDGE,"E48.1"),sQuery(id+"F22.wireOp",EDGE,"E48.2"),sQuery(id+"F22.wireOp",EDGE,"E48.3"),sQuery(id+"F22.wireOp",EDGE,"E48.4"),sQuery(id+"F22.wireOp",EDGE,"E48.5"),sQuery(id+"F22.wireOp",EDGE,"E48.6"),sQuery(id+"F22.wireOp",EDGE,"E49"),sQuery(id+"F22.wireOp",EDGE,"E50")])]});
            var Q3;
            Q3=makeQuery(id+"F32.opExtrude","SWEPT_BODY",BODY,{"disambiguationData":[OSD([sQuery(id+"F31.wireOp",EDGE,"E56.0.0"),sQuery(id+"F31.wireOp",EDGE,"E56.0.1"),sQuery(id+"F31.wireOp",EDGE,"E56.0.2"),sQuery(id+"F31.wireOp",EDGE,"E56.0.3")])]});
            hole(context, id + "F37", {"style" : HoleStyle.C_SINK, "endStyle" : HoleEndStyle.BLIND, "standardTappedOrClearance" : lookupTablePath({ "standard" : "ISO", "engagement" : "75%", "pitch" : "0.5 mm", "size" : "M3", "type" : "Tapped" }), "standardBlindInLast" : lookupTablePath({ "standard" : "ISO", "engagement" : "75%", "pitch" : "0.5 mm", "size" : "M3", "type" : "Tapped" }), "holeDiameter" : 2.5 * mm, "cSinkDiameter" : 6.72 * mm, "cSinkAngle" : 90 * degree, "showTappedDepth" : true, "holeDepth" : 13.5 * mm, "isTappedThrough" : true, "tappedDepth" : 12 * mm, "tapClearance" : 3, "locations" : qUnion([Q0, Q1]), "scope" : qUnion([Q2, Q3]), "majorDiameter" : 3 * mm});
        }
        {
            var Q0;
            Q0=sQuery(id+"F36.wireOp",VERTEX,"E58");
            var Q1;
            Q1=sQuery(id+"F36.wireOp",VERTEX,"E59");
            var Q2;
            Q2=makeQuery(id+"F32.opExtrude","SWEPT_BODY",BODY,{"disambiguationData":[OSD([sQuery(id+"F31.wireOp",EDGE,"E56.0.0"),sQuery(id+"F31.wireOp",EDGE,"E56.0.1"),sQuery(id+"F31.wireOp",EDGE,"E56.0.2"),sQuery(id+"F31.wireOp",EDGE,"E56.0.3")])]});
            hole(context, id + "F38", {"style" : HoleStyle.C_SINK, "endStyle" : HoleEndStyle.BLIND, "standardTappedOrClearance" : lookupTablePath({ "standard" : "ISO", "fit" : "Normal", "size" : "M3", "type" : "Clearance" }), "standardBlindInLast" : lookupTablePath({ "fit" : "Standard", "standard" : "ISO", "size" : "M3", "type" : "Clearance" }), "holeDiameter" : 3.3 * mm, "cSinkDiameter" : 6.72 * mm, "cSinkAngle" : 90 * degree, "holeDepth" : 13.5 * mm, "isTappedThrough" : true, "tappedDepth" : 12 * mm, "tapClearance" : 3, "locations" : qUnion([Q0, Q1]), "scope" : qUnion([Q2])});
        }
    });
